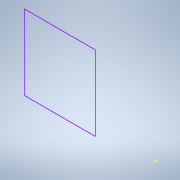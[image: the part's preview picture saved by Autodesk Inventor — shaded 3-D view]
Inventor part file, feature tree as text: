
AUTODESK INVENTOR PART (.ipt)
format: ipt  version: 2022 (Build 260153000, 153)  size: 253,952 bytes
history: native  units: in
note: dims shown in document units (in); Inventor stores cm internally (conversion verified against a paired STEP export)
features: reference x27, other x9, extrude x3, sketch x3, fillet x1, projected_geometry x1
ambient origin geometry x8: Origin, YZ Plane, XZ Plane, XY Plane, X Axis, Y Axis, Z Axis, Center Point
bodies: Solid1 (feature_tree)
feature tree (44):
  extrude  "Extrusion1"  Depth=0.3937in
  extrude  "Extrusion2"  Depth=8.6614in
  extrude  "Extrusion3"  Depth=0.1969in
  fillet  "Fillet1"  Radius=0.1575in
  sketch  "Sketch1"  dims[d0=0.3937in d1=0.0in d2=0.3937in]
  reference  "Reference1"
  sketch  "Sketch2"  dims[d3=8.5433in d4=8.6614in]
  projected_geometry  "Projected Loop1"
  reference  "Reference2"
  reference  "Reference3"
  reference  "Reference4"
  reference  "Reference5"
  reference  "Reference6"
  reference  "Reference7"
  reference  "Reference8"
  reference  "Reference9"
  reference  "Reference10"
  reference  "Reference11"
  reference  "Reference12"
  reference  "Reference13"
  reference  "Reference14"
  reference  "Reference15"
  reference  "Reference16"
  reference  "Reference17"
  reference  "Reference18"
  reference  "Reference19"
  reference  "Reference20"
  reference  "Reference21"
  reference  "Reference22"
  reference  "Reference23"
  reference  "Reference24"
  reference  "Reference25"
  sketch  "Sketch3"  dims[d5=0.1575in d6=0.1575in d7=0.1575in d8=0.1575in d9=0.0in d10=0.0in d11=0.1969in d12=0.1969in d13=3.937in d14=0.0in d15=0.1969in]
  reference  "Reference26"
  reference  "Reference27"
  other  "Linear Rail Assembly.iam"
  other  "TB6600 - Driver Motor de Passo 4A:2"
  other  "L298N:3"
  other  "L298N:2"
  other  "L298N:1"
  other  "Raspberry Pi 3:1"
  other  "Keyes KY 019 Montaj:1"
  other  "ArduinoMega_STEP_AP203:1"
  other  "TB6600 - Driver Motor de Passo 4A:1"
